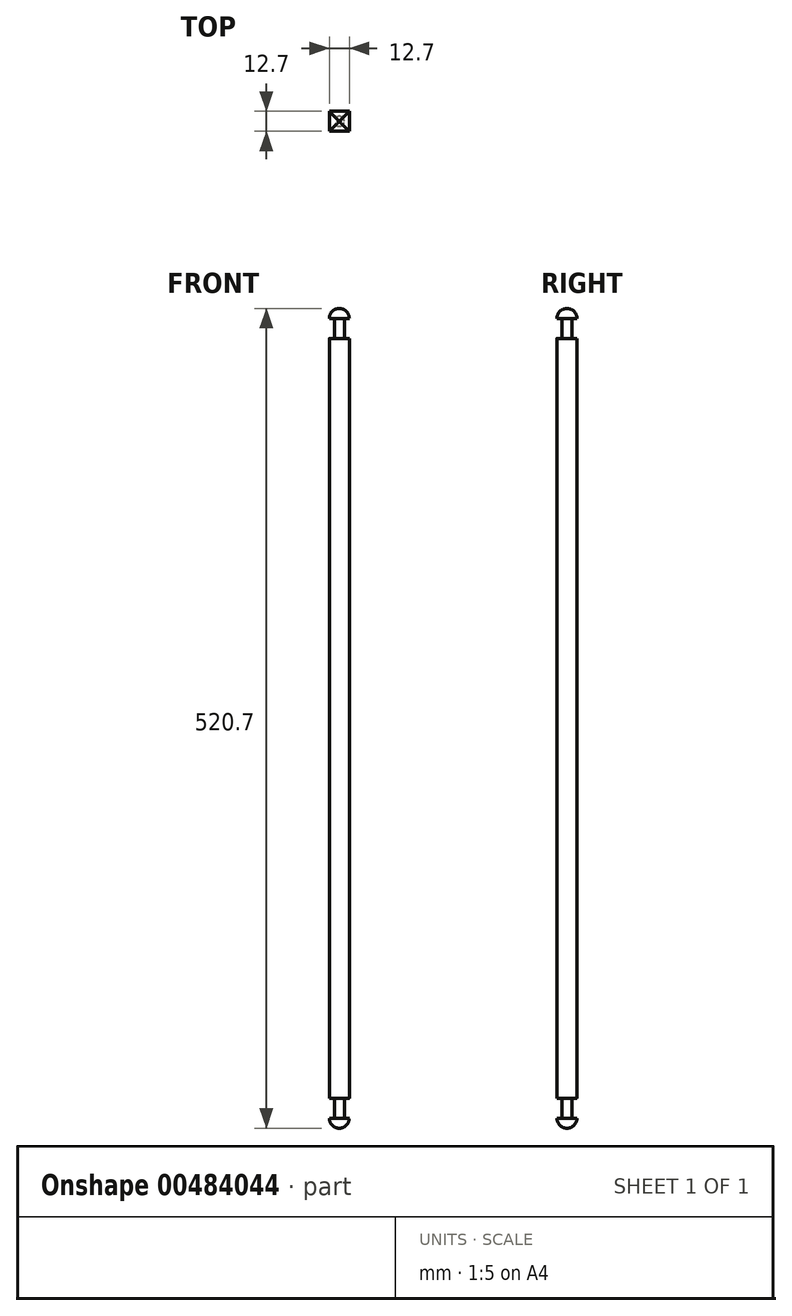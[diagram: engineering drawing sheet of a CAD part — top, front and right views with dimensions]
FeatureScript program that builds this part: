
annotation { "Feature Type Name" : "Feature", "Feature Type Description" : "" }
export const myFeature = defineFeature(function(context is Context, id is Id, definition is map)
    precondition{}
    {
        {
            var Q0;
            Q0=qCreatedBy(makeId("Top.planeOp"),FACE);
            var sketch = newSketch(context, id + "F0", { "sketchPlane" : qUnion([Q0])});
            skLineSegment(sketch, "E0.bottom", {"start": v(0, 0) * mm, "end": v(12.7, 0) * mm});
            skLineSegment(sketch, "E0.top", {"start": v(0, 12.7) * mm, "end": v(12.7, 12.7) * mm});
            skLineSegment(sketch, "E0.left", {"start": v(0, 0) * mm, "end": v(0, 12.7) * mm});
            skLineSegment(sketch, "E0.right", {"start": v(12.7, 0) * mm, "end": v(12.7, 12.7) * mm});
            skSolve(sketch);
        }
        {
            var Q0;
            Q0=makeQuery(id+"F0.imprint","IMPRINT",FACE,{"disambiguationData":[TD([[makeQuery(id+"F0.imprint","IMPRINT",EDGE,{"derivedFrom":sQuery(id+"F0.wireOp",EDGE,"E0.bottom")}),1.0]])]});
            extrude(context, id + "F1", {"entities" : qUnion([Q0]), "oppositeDirection" : true, "depth" : 482.6 * mm});
        }
        {
            var Q0;
            Q0=makeQuery(id+"F1.opExtrude","CAP_FACE",FACE,{"disambiguationData":[OSD([sQuery(id+"F0.wireOp",EDGE,"E0.bottom"),sQuery(id+"F0.wireOp",EDGE,"E0.top"),sQuery(id+"F0.wireOp",EDGE,"E0.left"),sQuery(id+"F0.wireOp",EDGE,"E0.right")])],"isStart":true});
            var sketch = newSketch(context, id + "F2", { "sketchPlane" : qUnion([Q0])});
            skCircle(sketch, "E1", {"center": v(6.35, 6.35) * mm, "radius": 3.18 * mm});
            skPoint(sketch, "E1.centerSnap0", {"position": v(12.7, 6.35) * mm});
            skPoint(sketch, "E1.centerSnap1", {"position": v(6.35, 12.7) * mm});
            skSolve(sketch);
        }
        {
            var Q0;
            Q0 = qSketchRegion(id + "F2", true);
            extrude(context, id + "F3", {"entities" : qUnion([Q0]), "operationType" : NewBodyOperationType.ADD, "depth" : 12.7 * mm});
        }
        {
            var Q0;
            Q0=makeQuery(id+"F1.opExtrude","CAP_FACE",FACE,{"disambiguationData":[OSD([sQuery(id+"F0.wireOp",EDGE,"E0.bottom"),sQuery(id+"F0.wireOp",EDGE,"E0.top"),sQuery(id+"F0.wireOp",EDGE,"E0.left"),sQuery(id+"F0.wireOp",EDGE,"E0.right")])],"isStart":false});
            var sketch = newSketch(context, id + "F4", { "sketchPlane" : qUnion([Q0])});
            skCircle(sketch, "E2", {"center": v(6.35, -6.35) * mm, "radius": 3.18 * mm});
            skPoint(sketch, "E2.centerSnap0", {"position": v(6.35, 0) * mm});
            skPoint(sketch, "E2.centerSnap1", {"position": v(12.7, -6.35) * mm});
            skSolve(sketch);
        }
        {
            var Q0;
            Q0 = qSketchRegion(id + "F4", true);
            extrude(context, id + "F5", {"entities" : qUnion([Q0]), "operationType" : NewBodyOperationType.ADD, "depth" : 12.7 * mm});
        }
        {
            var Q0;
            Q0=makeQuery(id+"F3.opExtrude","CAP_FACE",FACE,{"disambiguationData":[OSD([sQuery(id+"F2.wireOp",EDGE,"E1")])],"isStart":false});
            var sketch = newSketch(context, id + "F6", { "sketchPlane" : qUnion([Q0])});
            skLineSegment(sketch, "E3.bottom", {"start": v(0, 0) * mm, "end": v(12.7, 0) * mm});
            skLineSegment(sketch, "E3.top", {"start": v(0, 12.7) * mm, "end": v(12.7, 12.7) * mm});
            skLineSegment(sketch, "E3.left", {"start": v(0, 0) * mm, "end": v(0, 12.7) * mm});
            skLineSegment(sketch, "E3.right", {"start": v(12.7, 0) * mm, "end": v(12.7, 12.7) * mm});
            skSolve(sketch);
        }
        {
            var Q0;
            Q0 = qSketchRegion(id + "F6", true);
            extrude(context, id + "F7", {"entities" : qUnion([Q0]), "operationType" : NewBodyOperationType.ADD, "depth" : 6.35 * mm});
        }
        {
            var Q0;
            Q0=makeQuery(id+"F7.opExtrude","CAP_EDGE",EDGE,{"disambiguationData":[OSD([sQuery(id+"F6.wireOp",EDGE,"E3.left")])],"isStart":false});
            var Q1;
            Q1=makeQuery(id+"F7.opExtrude","CAP_FACE",FACE,{"disambiguationData":[OSD([sQuery(id+"F6.wireOp",EDGE,"E3.bottom"),sQuery(id+"F6.wireOp",EDGE,"E3.top"),sQuery(id+"F6.wireOp",EDGE,"E3.left"),sQuery(id+"F6.wireOp",EDGE,"E3.right")])],"isStart":false});
            fillet(context, id + "F8", {"entities" : qUnion([Q0, Q1]), "radius" : 6.35 * mm, "tangentPropagation" : true, "allowEdgeOverflow" : false});
        }
        {
            var Q0;
            Q0=makeQuery(id+"F5.opExtrude","CAP_FACE",FACE,{"disambiguationData":[OSD([sQuery(id+"F4.wireOp",EDGE,"E2")])],"isStart":false});
            var sketch = newSketch(context, id + "F9", { "sketchPlane" : qUnion([Q0])});
            skLineSegment(sketch, "E4.bottom", {"start": v(0, 0) * mm, "end": v(12.7, 0) * mm});
            skLineSegment(sketch, "E4.top", {"start": v(0, -12.7) * mm, "end": v(12.7, -12.7) * mm});
            skLineSegment(sketch, "E4.left", {"start": v(0, 0) * mm, "end": v(0, -12.7) * mm});
            skLineSegment(sketch, "E4.right", {"start": v(12.7, 0) * mm, "end": v(12.7, -12.7) * mm});
            skSolve(sketch);
        }
        {
            var Q0;
            Q0 = qSketchRegion(id + "F9", true);
            extrude(context, id + "F10", {"entities" : qUnion([Q0]), "operationType" : NewBodyOperationType.ADD, "depth" : 6.35 * mm});
        }
        {
            var Q0;
            Q0=makeQuery(id+"F10.opExtrude","CAP_FACE",FACE,{"disambiguationData":[OSD([sQuery(id+"F9.wireOp",EDGE,"E4.bottom"),sQuery(id+"F9.wireOp",EDGE,"E4.top"),sQuery(id+"F9.wireOp",EDGE,"E4.left"),sQuery(id+"F9.wireOp",EDGE,"E4.right")])],"isStart":false});
            fillet(context, id + "F11", {"entities" : qUnion([Q0]), "radius" : 6.35 * mm, "tangentPropagation" : true, "allowEdgeOverflow" : false});
        }
        {
            var Q0;
            Q0=makeQuery(id+"F1.opExtrude","SWEPT_EDGE",EDGE,{"disambiguationData":[OSD([sQuery(id+"F0.wireOp",EDGE,"E0.bottom"),sQuery(id+"F0.wireOp",EDGE,"E0.left")])]});
            var Q1;
            Q1=makeQuery(id+"F1.opExtrude","SWEPT_EDGE",EDGE,{"disambiguationData":[OSD([sQuery(id+"F0.wireOp",EDGE,"E0.top"),sQuery(id+"F0.wireOp",EDGE,"E0.left")])]});
            var Q2;
            Q2=makeQuery(id+"F1.opExtrude","SWEPT_EDGE",EDGE,{"disambiguationData":[OSD([sQuery(id+"F0.wireOp",EDGE,"E0.bottom"),sQuery(id+"F0.wireOp",EDGE,"E0.right")])]});
            var Q3;
            Q3=makeQuery(id+"F1.opExtrude","SWEPT_EDGE",EDGE,{"disambiguationData":[OSD([sQuery(id+"F0.wireOp",EDGE,"E0.top"),sQuery(id+"F0.wireOp",EDGE,"E0.right")])]});
            fillet(context, id + "F12", {"entities" : qUnion([Q0, Q1, Q2, Q3]), "radius" : 1.59 * mm, "tangentPropagation" : true, "allowEdgeOverflow" : false});
        }
    });
